# Revit family: Detail-Shades-Hunter_Douglas-RB500-Standard_Duty-Clutch-Bracket-38
name_source: partatom
category: Detail Items
units: mm (PartAtom-declared; Revit-internal decimal feet)

## family parameters
OmniClass Number = 23.30.60.14
OmniClass Title = Interior Window Treatment
Rotate with component = No
Section Shape = Not Defined
Shared = No

## types (2) — shared parameters
Assembly Code = E2010300
CD_Height = 2 27/32"
CD_Install Documentation = https://www.hunterdouglasarchitectural.com
CD_Microsite = https://microsite.caddetails.com
CD_Product Documentation Link = https://www.hunterdouglasarchitectural.com
CD_Product Name = RB 500 Roller Shade System
CD_Product Page URL = https://www.hunterdouglasarchitectural.com
CD_Warranty = https://assets.hunterdouglasarchitectural.com
CD_Width = 2 27/32"
Description = Standard Duty Roller Shade
Manufacturer = Hunter Douglas Architectural
Model = Standard Clutch 38 Bracket
URL = https://www.hunterdouglasarchitectural.com

## per-type parameters (varying)
| type | CD_Side Mount | CD_Top Mount | Type Comments |
| Top Mount | No | Yes | Ceiling Mounted/Inside Mounted |
| Side Mount | Yes | No | Face Mounted/Wall Mounted |

## geometry (parser evidence)
native form markers: Sweep x2
no freeform markers — native parametric forms only
